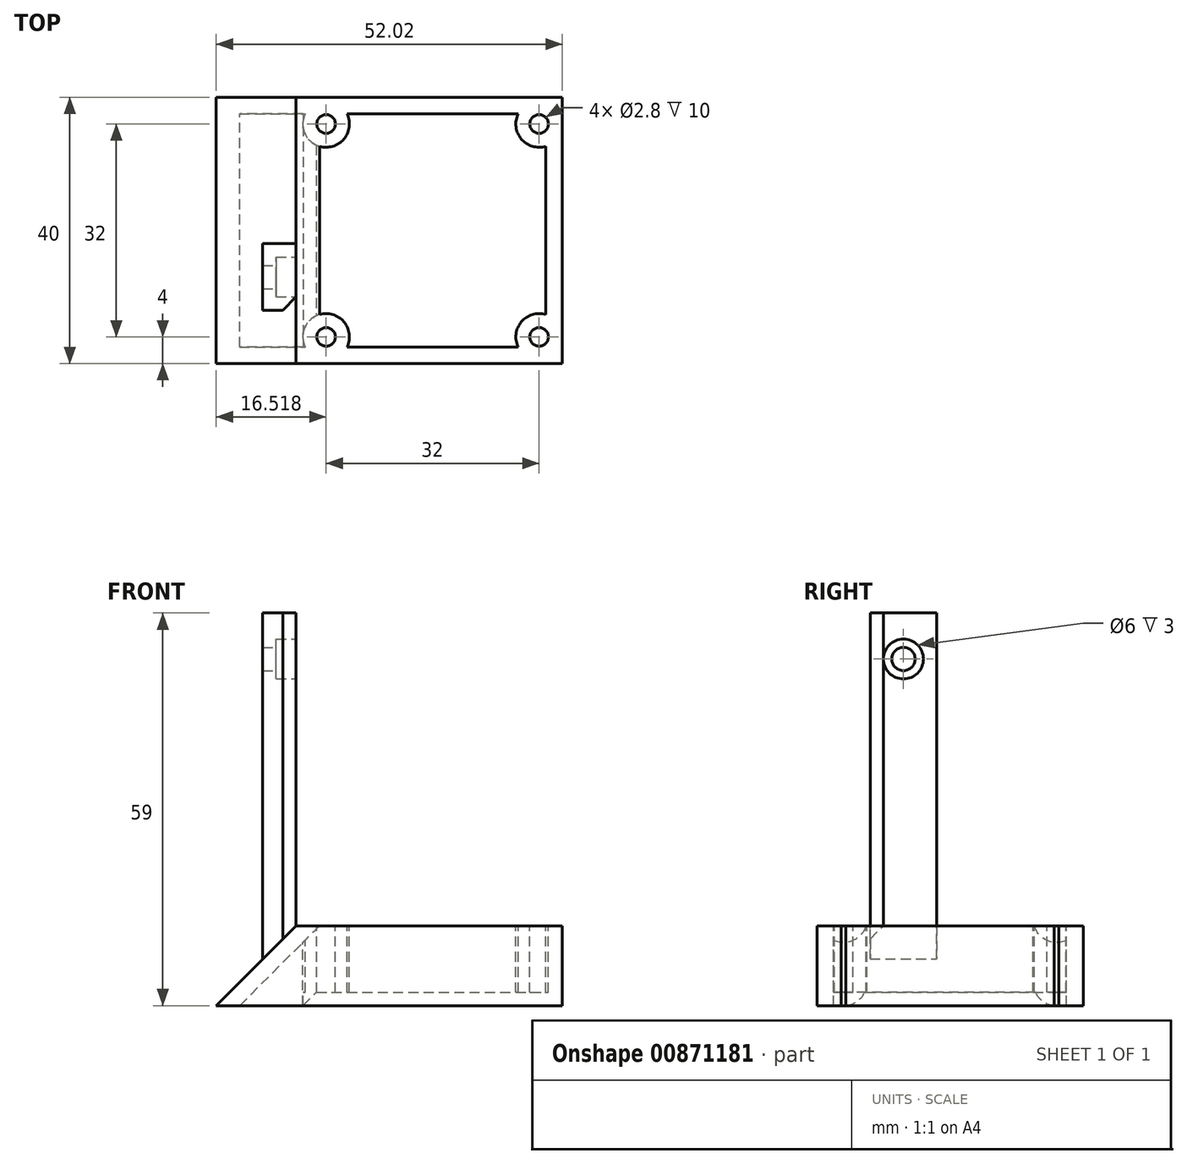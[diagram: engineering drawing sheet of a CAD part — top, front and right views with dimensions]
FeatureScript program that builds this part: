
annotation { "Feature Type Name" : "Feature", "Feature Type Description" : "" }
export const myFeature = defineFeature(function(context is Context, id is Id, definition is map)
    precondition{}
    {
        {
            var Q0;
            Q0=qCreatedBy(makeId("Front.planeOp"),FACE);
            var sketch = newSketch(context, id + "F0", { "sketchPlane" : qUnion([Q0])});
            skLineSegment(sketch, "E0", {"start": v(0, 0) * mm, "end": v(12, 12) * mm});
            skLineSegment(sketch, "E1", {"start": v(12, 12) * mm, "end": v(52, 12) * mm});
            skLineSegment(sketch, "E2", {"start": v(52, 12) * mm, "end": v(52, 0) * mm});
            skLineSegment(sketch, "E3", {"start": v(52, 0) * mm, "end": v(0, 0) * mm});
            skSolve(sketch);
        }
        {
            var Q0;
            Q0 = qSketchRegion(id + "F0", true);
            extrude(context, id + "F1", {"entities" : qUnion([Q0]), "depth" : 40 * mm, "offsetDistance" : 25 * mm});
        }
        {
            var Q0;
            Q0=makeQuery(id+"F1.opExtrude","SWEPT_FACE",FACE,{"disambiguationData":[OSD([sQuery(id+"F0.wireOp",EDGE,"E1")])]});
            var Q1;
            Q1=makeQuery(id+"F1.opExtrude","SWEPT_FACE",FACE,{"disambiguationData":[OSD([sQuery(id+"F0.wireOp",EDGE,"E3")])]});
            shell(context, id + "F2", {"entities" : qUnion([Q0, Q1]), "thickness" : 2.5 * mm});
        }
        {
            var Q0;
            Q0=makeQuery(id+"F1.opExtrude","SWEPT_FACE",FACE,{"disambiguationData":[OSD([sQuery(id+"F0.wireOp",EDGE,"E1")])]});
            var sketch = newSketch(context, id + "F3", { "sketchPlane" : qUnion([Q0])});
            skLineSegment(sketch, "E4.bottom", {"start": v(48.52, -4) * mm, "end": v(16.52, -4) * mm, "construction": true});
            skLineSegment(sketch, "E4.top", {"start": v(48.52, -36) * mm, "end": v(16.52, -36) * mm, "construction": true});
            skLineSegment(sketch, "E4.left", {"start": v(48.52, -4) * mm, "end": v(48.52, -36) * mm, "construction": true});
            skLineSegment(sketch, "E4.right", {"start": v(16.52, -4) * mm, "end": v(16.52, -36) * mm, "construction": true});
            skPoint(sketch, "E4.middle", {"position": v(32.52, -20) * mm});
            skPoint(sketch, "E5", {"position": v(15.54, -20) * mm});
            skPoint(sketch, "E6", {"position": v(32.52, -37.5) * mm});
            skCircle(sketch, "E7", {"center": v(16.52, -36) * mm, "radius": 3.5 * mm});
            skCircle(sketch, "E8", {"center": v(48.52, -36) * mm, "radius": 3.5 * mm});
            skCircle(sketch, "E9", {"center": v(48.52, -4) * mm, "radius": 3.5 * mm});
            skCircle(sketch, "E10", {"center": v(16.52, -4) * mm, "radius": 3.5 * mm});
            skSolve(sketch);
        }
        {
            var Q0;
            Q0 = qSketchRegion(id + "F3", true);
            var Q1;
            Q1=makeQuery(id+"F1.opExtrude","SWEPT_FACE",FACE,{"disambiguationData":[OSD([sQuery(id+"F0.wireOp",EDGE,"E3")])]});
            extrude(context, id + "F4", {"entities" : qUnion([Q0]), "operationType" : NewBodyOperationType.ADD, "endBound" : BoundingType.UP_TO_SURFACE, "oppositeDirection" : true, "depth" : 25 * mm, "endBoundEntityFace" : qUnion([Q1]), "offsetDistance" : 25 * mm});
        }
        {
            var Q0;
            Q0=makeQuery(id+"F4.boolean.opBoolean","MERGE",FACE,{"derivedFrom":[makeQuery(id+"F1.opExtrude","SWEPT_FACE",FACE,{"disambiguationData":[OSD([sQuery(id+"F0.wireOp",EDGE,"E1")])]}),makeQuery(id+"F4.opExtrude","CAP_FACE",FACE,{"disambiguationData":[OSD([sQuery(id+"F3.wireOp",EDGE,"E7")])],"isStart":true}),makeQuery(id+"F4.opExtrude","CAP_FACE",FACE,{"disambiguationData":[OSD([sQuery(id+"F3.wireOp",EDGE,"E8")])],"isStart":true}),makeQuery(id+"F4.opExtrude","CAP_FACE",FACE,{"disambiguationData":[OSD([sQuery(id+"F3.wireOp",EDGE,"E9")])],"isStart":true}),makeQuery(id+"F4.opExtrude","CAP_FACE",FACE,{"disambiguationData":[OSD([sQuery(id+"F3.wireOp",EDGE,"E10")])],"isStart":true})]});
            var sketch = newSketch(context, id + "F5", { "sketchPlane" : qUnion([Q0])});
            skCircle(sketch, "E11", {"center": v(16.52, -4) * mm, "radius": 1.4 * mm});
            skCircle(sketch, "E12", {"center": v(48.52, -4) * mm, "radius": 1.4 * mm});
            skCircle(sketch, "E13", {"center": v(48.52, -36) * mm, "radius": 1.4 * mm});
            skCircle(sketch, "E14", {"center": v(16.52, -36) * mm, "radius": 1.4 * mm});
            skSolve(sketch);
        }
        {
            var Q0;
            Q0 = qSketchRegion(id + "F5", true);
            extrude(context, id + "F6", {"entities" : qUnion([Q0]), "operationType" : NewBodyOperationType.REMOVE, "endBound" : BoundingType.THROUGH_ALL, "oppositeDirection" : true, "depth" : 25 * mm, "offsetDistance" : 25 * mm});
        }
        {
            var Q0;
            {var subQ0=sQuery(id+"F0.wireOp",EDGE,"E3");Q0=makeQuery(id+"F4.boolean.opBoolean","MERGE",FACE,{"derivedFrom":[makeQuery(id+"F1.opExtrude","SWEPT_FACE",FACE,{"disambiguationData":[OSD([subQ0])]}),makeQuery(id+"F4.opExtrude","CAP_FACE",FACE,{"disambiguationData":[OSD([subQ0]),OD(0.0)],"isStart":false}),makeQuery(id+"F4.opExtrude","CAP_FACE",FACE,{"disambiguationData":[OSD([subQ0]),OD(1.0)],"isStart":false}),makeQuery(id+"F4.opExtrude","CAP_FACE",FACE,{"disambiguationData":[OSD([subQ0]),OD(2.0)],"isStart":false}),makeQuery(id+"F4.opExtrude","CAP_FACE",FACE,{"disambiguationData":[OSD([subQ0]),OD(3.0)],"isStart":false})]});}
            var sketch = newSketch(context, id + "F7", { "sketchPlane" : qUnion([Q0])});
            skLineSegment(sketch, "E15.bottom", {"start": v(52, 0) * mm, "end": v(13.04, 0) * mm});
            skLineSegment(sketch, "E15.top", {"start": v(52, 40) * mm, "end": v(13.04, 40) * mm});
            skLineSegment(sketch, "E15.left", {"start": v(52, 0) * mm, "end": v(52, 40) * mm});
            skLineSegment(sketch, "E15.right", {"start": v(13.04, 0) * mm, "end": v(13.04, 40) * mm});
            skSolve(sketch);
        }
        {
            var Q0;
            Q0 = qSketchRegion(id + "F7", true);
            extrude(context, id + "F8", {"entities" : qUnion([Q0]), "operationType" : NewBodyOperationType.ADD, "oppositeDirection" : true, "depth" : 2 * mm, "offsetDistance" : 25 * mm});
        }
        {
            var Q0;
            {var subQ0=sQuery(id+"F7.wireOp",EDGE,"E15.right");Q0=makeQuery(id+"F8.boolean.opBoolean","SPLIT",EDGE,{"disambiguationData":[TD([makeQuery(id+"F4.opExtrude","SWEPT_FACE",FACE,{"disambiguationData":[OSD([sQuery(id+"F3.wireOp",EDGE,"E7")])]}),makeQuery(id+"F4.opExtrude","SWEPT_FACE",FACE,{"disambiguationData":[OSD([sQuery(id+"F3.wireOp",EDGE,"E10")])]}),makeQuery(id+"F8.opExtrude","CAP_FACE",FACE,{"disambiguationData":[OSD([sQuery(id+"F7.wireOp",EDGE,"E15.bottom"),sQuery(id+"F7.wireOp",EDGE,"E15.top"),sQuery(id+"F7.wireOp",EDGE,"E15.left"),subQ0])],"isStart":false}),makeQuery(id+"F8.opExtrude","SWEPT_FACE",FACE,{"disambiguationData":[OSD([subQ0])]})])],"derivedFrom":makeQuery(id+"F8.opExtrude","CAP_EDGE",EDGE,{"disambiguationData":[OSD([subQ0])],"isStart":false})});}
            chamfer(context, id + "F9", {"entities" : qUnion([Q0]), "width" : 2 * mm, "tangentPropagation" : true});
        }
        {
            var Q0;
            Q0=qCreatedBy(makeId("Front.planeOp"),FACE);
            cPlane(context, id + "F10", {"entities" : qUnion([Q0]), "cplaneType" : CPlaneType.OFFSET, "offset" : 27 * mm, "width" : 150 * mm, "height" : 150 * mm});
        }
        {
            var Q0;
            Q0=qCreatedBy(id+"F10.planeOp",FACE);
            var sketch = newSketch(context, id + "F11", { "sketchPlane" : qUnion([Q0])});
            skLineSegment(sketch, "E16", {"start": v(7, 7) * mm, "end": v(7, 59) * mm});
            skLineSegment(sketch, "E17", {"start": v(7, 59) * mm, "end": v(12, 59) * mm});
            skLineSegment(sketch, "E18", {"start": v(12, 59) * mm, "end": v(12, 12) * mm});
            skLineSegment(sketch, "E19", {"start": v(12, 12) * mm, "end": v(7, 7) * mm});
            skSolve(sketch);
        }
        {
            var Q0;
            Q0 = qSketchRegion(id + "F11", true);
            extrude(context, id + "F12", {"entities" : qUnion([Q0]), "operationType" : NewBodyOperationType.ADD, "endBound" : BoundingType.SYMMETRIC, "depth" : 10 * mm, "offsetDistance" : 25 * mm});
        }
        {
            var Q0;
            Q0=makeQuery(id+"F12.opExtrude","SWEPT_FACE",FACE,{"disambiguationData":[OSD([sQuery(id+"F11.wireOp",EDGE,"E18")])]});
            var sketch = newSketch(context, id + "F13", { "sketchPlane" : qUnion([Q0])});
            skCircle(sketch, "E20", {"center": v(-27, 52.1) * mm, "radius": 1.75 * mm});
            skSolve(sketch);
        }
        {
            var Q0;
            Q0 = qSketchRegion(id + "F13", true);
            extrude(context, id + "F14", {"entities" : qUnion([Q0]), "operationType" : NewBodyOperationType.REMOVE, "endBound" : BoundingType.THROUGH_ALL, "oppositeDirection" : true, "depth" : 25 * mm, "offsetDistance" : 25 * mm});
        }
        {
            var Q0;
            Q0=makeQuery(id+"F12.opExtrude","SWEPT_FACE",FACE,{"disambiguationData":[OSD([sQuery(id+"F11.wireOp",EDGE,"E18")])]});
            var sketch = newSketch(context, id + "F15", { "sketchPlane" : qUnion([Q0])});
            skCircle(sketch, "E21", {"center": v(-27, 52.1) * mm, "radius": 3 * mm});
            skSolve(sketch);
        }
        {
            var Q0;
            Q0 = qSketchRegion(id + "F15", true);
            extrude(context, id + "F16", {"entities" : qUnion([Q0]), "operationType" : NewBodyOperationType.REMOVE, "oppositeDirection" : true, "depth" : 3 * mm, "offsetDistance" : 25 * mm});
        }
        {
            var Q0;
            Q0=makeQuery(id+"F12.opExtrude","CAP_EDGE",EDGE,{"disambiguationData":[OSD([sQuery(id+"F11.wireOp",EDGE,"E18")])],"isStart":false});
            chamfer(context, id + "F17", {"entities" : qUnion([Q0]), "width" : 2 * mm, "tangentPropagation" : true});
        }
    });
